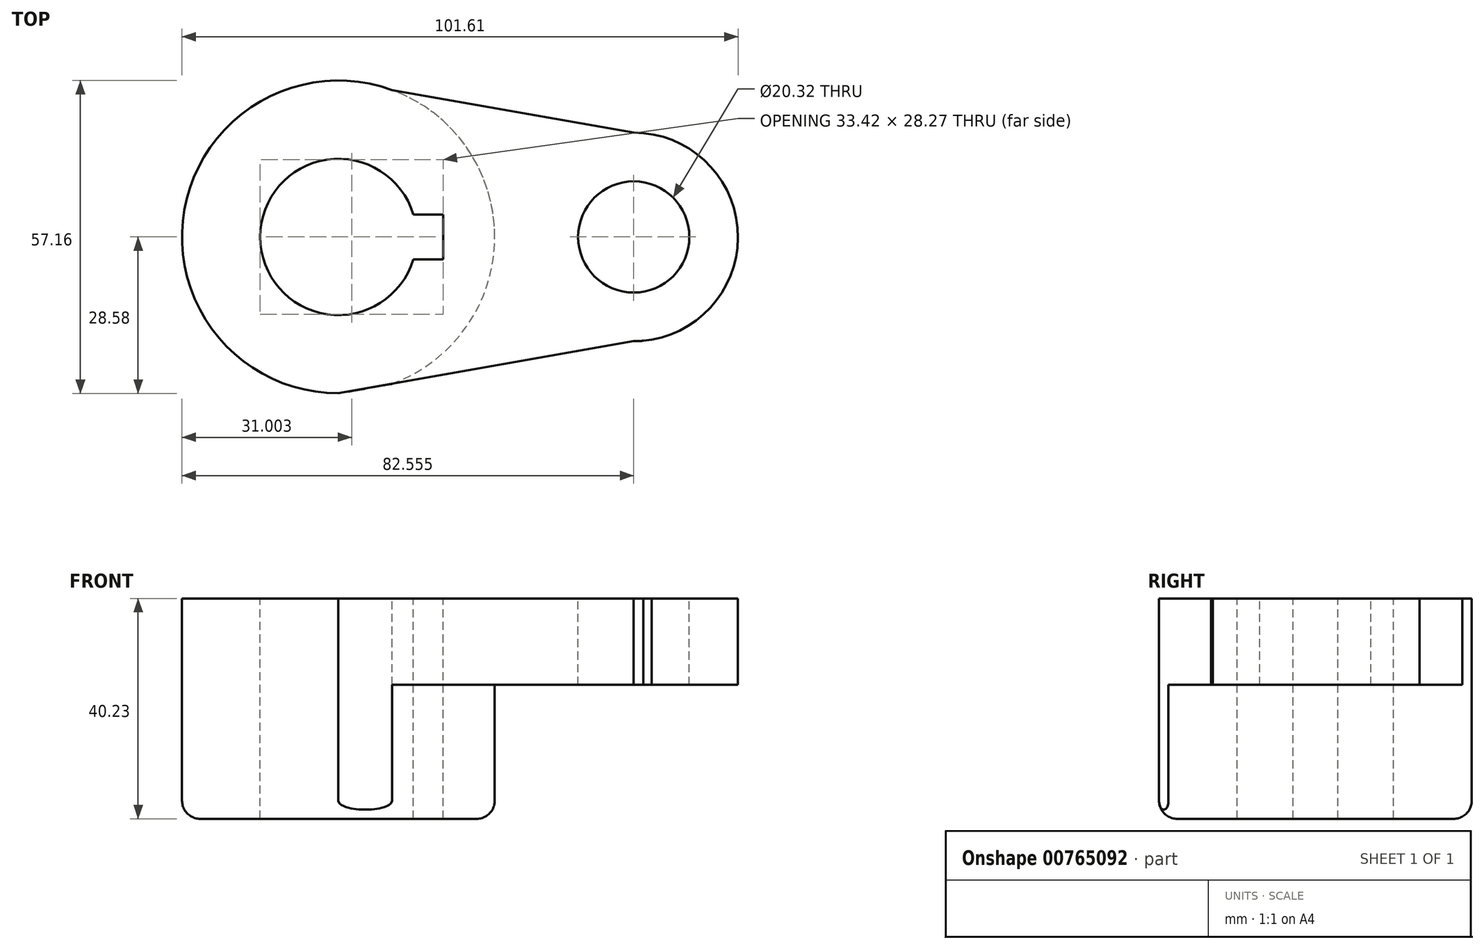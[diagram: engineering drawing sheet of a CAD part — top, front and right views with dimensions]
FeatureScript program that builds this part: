
annotation { "Feature Type Name" : "Feature", "Feature Type Description" : "" }
export const myFeature = defineFeature(function(context is Context, id is Id, definition is map)
    precondition{}
    {
        {
            var Q0;
            Q0=qCreatedBy(makeId("Top.planeOp"),FACE);
            var sketch = newSketch(context, id + "F0", { "sketchPlane" : qUnion([Q0])});
            skCircle(sketch, "E0", {"center": v(0, 0) * mm, "radius": 28.58 * mm});
            skArc(sketch, "E1", {"start": v(13.68, 4.11) * mm, "mid": v(-14.29, 0) * mm, "end": v(13.68, -4.11) * mm});
            skLineSegment(sketch, "E2.bottom", {"start": v(13.68, 4.11) * mm, "end": v(19.13, 4.11) * mm});
            skLineSegment(sketch, "E2.top", {"start": v(13.68, -4.11) * mm, "end": v(19.13, -4.11) * mm});
            skLineSegment(sketch, "E2.right", {"start": v(19.13, 4.11) * mm, "end": v(19.13, -4.11) * mm});
            skPoint(sketch, "E3.orphan", {"position": v(-19.13, 4.11) * mm});
            skPoint(sketch, "E4.orphan", {"position": v(-19.13, -4.11) * mm});
            skLineSegment(sketch, "E5.left", {"start": v(17.45, 22.63) * mm, "end": v(17.45, 22.95) * mm});
            skCircle(sketch, "E6", {"center": v(53.98, 0) * mm, "radius": 10.16 * mm});
            skArc(sketch, "E7", {"start": v(53.97, -19.05) * mm, "mid": v(73.03, 0) * mm, "end": v(53.98, 19.05) * mm});
            skLineSegment(sketch, "E8", {"start": v(55.75, -18.97) * mm, "end": v(57.26, -18.76) * mm});
            skLineSegment(sketch, "E9", {"start": v(9.78, 26.85) * mm, "end": v(53.98, 19.05) * mm});
            skLineSegment(sketch, "E10", {"start": v(0, -28.58) * mm, "end": v(53.97, -19.05) * mm});
            skPoint(sketch, "E11.orphan", {"position": v(0, 28.58) * mm});
            skSolve(sketch);
        }
        {
            var Q0;
            Q0=makeQuery(id+"F0.imprint","IMPRINT",FACE,{"disambiguationData":[TD([[makeQuery(id+"F0.imprint","IMPRINT",EDGE,{"derivedFrom":sQuery(id+"F0.wireOp",EDGE,"E1")}),-1.0]])]});
            extrude(context, id + "F1", {"entities" : qUnion([Q0]), "oppositeDirection" : true, "depth" : 40.23 * mm, "offsetDistance" : 25.4 * mm});
        }
        {
            var Q0;
            Q0=makeQuery(id+"F0.imprint","IMPRINT",FACE,{"disambiguationData":[TD([[makeQuery(id+"F0.imprint","IMPRINT",EDGE,{"derivedFrom":sQuery(id+"F0.wireOp",EDGE,"E6")}),-1.0]])]});
            extrude(context, id + "F2", {"entities" : qUnion([Q0]), "operationType" : NewBodyOperationType.ADD, "oppositeDirection" : true, "depth" : 15.77 * mm, "offsetDistance" : 25.4 * mm});
        }
        {
            var Q0;
            Q0=makeQuery(id+"F1.opExtrude","CAP_EDGE",EDGE,{"disambiguationData":[OSD([sQuery(id+"F0.wireOp",EDGE,"E0")])],"isStart":false});
            fillet(context, id + "F3", {"entities" : qUnion([Q0]), "radius" : 3.3 * mm, "tangentPropagation" : true, "allowEdgeOverflow" : false});
        }
    });
